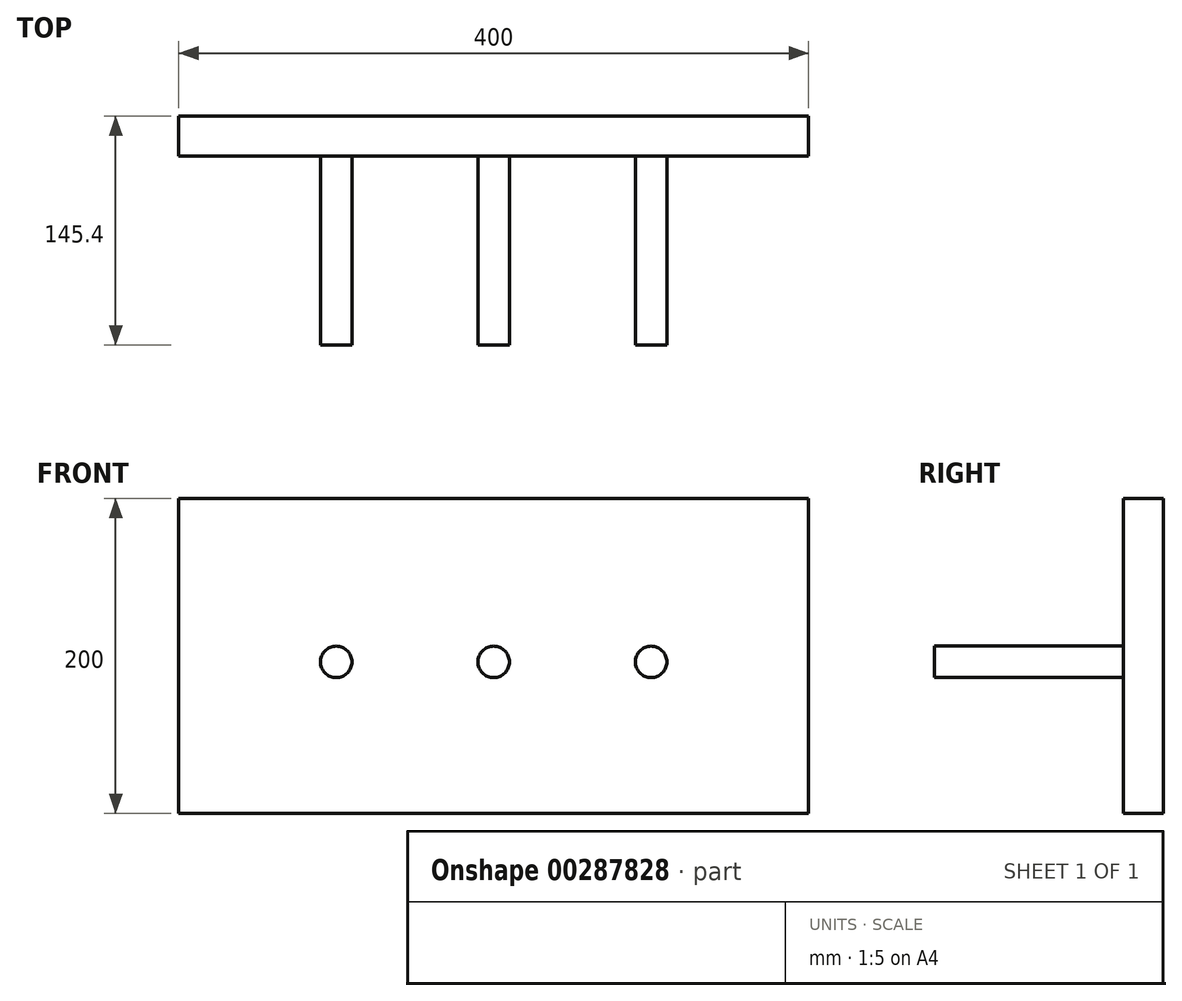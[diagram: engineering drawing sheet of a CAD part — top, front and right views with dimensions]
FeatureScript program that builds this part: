
annotation { "Feature Type Name" : "Feature", "Feature Type Description" : "" }
export const myFeature = defineFeature(function(context is Context, id is Id, definition is map)
    precondition{}
    {
        {
            var Q0;
            Q0=qCreatedBy(makeId("Front.planeOp"),FACE);
            var sketch = newSketch(context, id + "F0", { "sketchPlane" : qUnion([Q0])});
            skLineSegment(sketch, "E0.bottom", {"start": v(-235.92, 103.76) * mm, "end": v(164.08, 103.76) * mm});
            skLineSegment(sketch, "E0.top", {"start": v(-235.92, -96.24) * mm, "end": v(164.08, -96.24) * mm});
            skLineSegment(sketch, "E0.left", {"start": v(-235.92, 103.76) * mm, "end": v(-235.92, -96.24) * mm});
            skLineSegment(sketch, "E0.right", {"start": v(164.08, 103.76) * mm, "end": v(164.08, -96.24) * mm});
            skSolve(sketch);
        }
        {
            var Q0;
            Q0 = qSketchRegion(id + "F0", true);
            extrude(context, id + "F1", {"entities" : qUnion([Q0]), "depth" : 25.4 * mm});
        }
        {
            var Q0;
            Q0=makeQuery(id+"F1.opExtrude","CAP_FACE",FACE,{"disambiguationData":[OSD([sQuery(id+"F0.wireOp",EDGE,"E0.bottom"),sQuery(id+"F0.wireOp",EDGE,"E0.top"),sQuery(id+"F0.wireOp",EDGE,"E0.left"),sQuery(id+"F0.wireOp",EDGE,"E0.right")])],"isStart":false});
            var sketch = newSketch(context, id + "F2", { "sketchPlane" : qUnion([Q0])});
            skLineSegment(sketch, "E1", {"start": v(-235.92, 0) * mm, "end": v(-135.92, 0) * mm, "construction": true});
            skPoint(sketch, "E1.startSnap0", {"position": v(-235.92, 3.76) * mm});
            skCircle(sketch, "E2", {"center": v(-135.92, 0) * mm, "radius": 10 * mm});
            skLineSegment(sketch, "E3", {"start": v(-135.92, 0) * mm, "end": v(-35.92, 0) * mm, "construction": true});
            skCircle(sketch, "E4", {"center": v(-35.92, 0) * mm, "radius": 10 * mm});
            skLineSegment(sketch, "E5", {"start": v(-35.92, 0) * mm, "end": v(64.08, 0) * mm, "construction": true});
            skCircle(sketch, "E6", {"center": v(64.08, 0) * mm, "radius": 10 * mm});
            skLineSegment(sketch, "E7", {"start": v(64.08, 0) * mm, "end": v(164.08, 0) * mm});
            skSolve(sketch);
        }
        {
            var Q0;
            Q0 = qSketchRegion(id + "F2", true);
            extrude(context, id + "F3", {"entities" : qUnion([Q0]), "operationType" : NewBodyOperationType.ADD, "depth" : 120 * mm});
        }
    });
